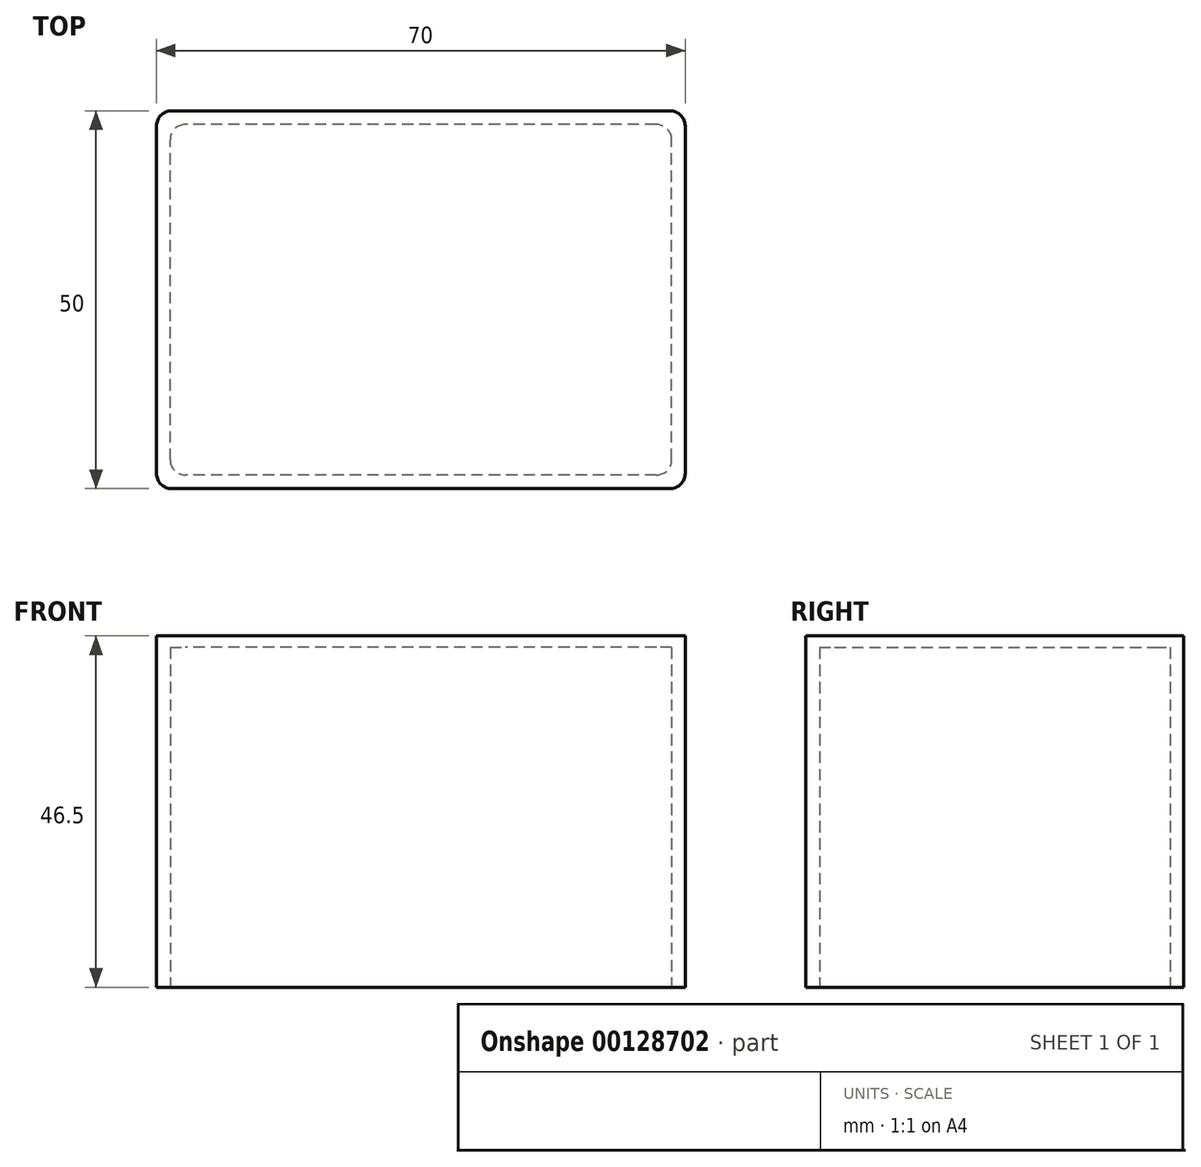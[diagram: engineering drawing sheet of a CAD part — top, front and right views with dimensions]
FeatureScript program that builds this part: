
annotation { "Feature Type Name" : "Feature", "Feature Type Description" : "" }
export const myFeature = defineFeature(function(context is Context, id is Id, definition is map)
    precondition{}
    {
        {
            var Q0;
            Q0=qCreatedBy(makeId("Top.planeOp"),FACE);
            var sketch = newSketch(context, id + "F0", { "sketchPlane" : qUnion([Q0])});
            skLineSegment(sketch, "E0.bottom", {"start": v(33, -25) * mm, "end": v(-33, -25) * mm});
            skLineSegment(sketch, "E0.top", {"start": v(33, 25) * mm, "end": v(-33, 25) * mm});
            skLineSegment(sketch, "E0.left", {"start": v(35, -23) * mm, "end": v(35, 23) * mm});
            skLineSegment(sketch, "E0.right", {"start": v(-35, -23) * mm, "end": v(-35, 23) * mm});
            skPoint(sketch, "E0.middle", {"position": v(0, 0) * mm});
            skLineSegment(sketch, "E1.0", {"start": v(31.2, 23.2) * mm, "end": v(-31.2, 23.2) * mm});
            skLineSegment(sketch, "E1.1", {"start": v(33.2, -21.2) * mm, "end": v(33.2, 21.2) * mm});
            skLineSegment(sketch, "E1.2", {"start": v(31.2, -23.2) * mm, "end": v(-31.2, -23.2) * mm});
            skLineSegment(sketch, "E1.3", {"start": v(-33.2, -21.2) * mm, "end": v(-33.2, 21.2) * mm});
            skPoint(sketch, "E2.visualSharp", {"position": v(-33.2, 23.2) * mm});
            skArc(sketch, "E2.filletArc", {"start": v(-31.2, 23.2) * mm, "mid": v(-32.61, 22.61) * mm, "end": v(-33.2, 21.2) * mm});
            skPoint(sketch, "E3.visualSharp", {"position": v(-35, 25) * mm});
            skArc(sketch, "E3.filletArc", {"start": v(-33, 25) * mm, "mid": v(-34.41, 24.41) * mm, "end": v(-35, 23) * mm});
            skPoint(sketch, "E4.visualSharp", {"position": v(33.2, 23.2) * mm});
            skArc(sketch, "E4.filletArc", {"start": v(33.2, 21.2) * mm, "mid": v(32.61, 22.61) * mm, "end": v(31.2, 23.2) * mm});
            skPoint(sketch, "E5.visualSharp", {"position": v(35, 25) * mm});
            skArc(sketch, "E5.filletArc", {"start": v(35, 23) * mm, "mid": v(34.41, 24.41) * mm, "end": v(33, 25) * mm});
            skPoint(sketch, "E6.visualSharp", {"position": v(33.2, -23.2) * mm});
            skArc(sketch, "E6.filletArc", {"start": v(31.2, -23.2) * mm, "mid": v(32.61, -22.61) * mm, "end": v(33.2, -21.2) * mm});
            skPoint(sketch, "E7.visualSharp", {"position": v(35, -25) * mm});
            skArc(sketch, "E7.filletArc", {"start": v(33, -25) * mm, "mid": v(34.41, -24.41) * mm, "end": v(35, -23) * mm});
            skPoint(sketch, "E8.visualSharp", {"position": v(-33.2, -23.2) * mm});
            skArc(sketch, "E8.filletArc", {"start": v(-33.2, -21.2) * mm, "mid": v(-32.61, -22.61) * mm, "end": v(-31.2, -23.2) * mm});
            skPoint(sketch, "E9.visualSharp", {"position": v(-35, -25) * mm});
            skArc(sketch, "E9.filletArc", {"start": v(-35, -23) * mm, "mid": v(-34.41, -24.41) * mm, "end": v(-33, -25) * mm});
            skSolve(sketch);
        }
        {
            var Q0;
            Q0=makeQuery(id+"F0.imprint","IMPRINT",FACE,{"disambiguationData":[TD([[makeQuery(id+"F0.imprint","IMPRINT",EDGE,{"derivedFrom":sQuery(id+"F0.wireOp",EDGE,"E0.bottom")}),-1.0]])]});
            extrude(context, id + "F1", {"entities" : qUnion([Q0]), "depth" : 45 * mm});
        }
        {
            var Q0;
            Q0=makeQuery(id+"F1.opExtrude","CAP_FACE",FACE,{"disambiguationData":[OSD([sQuery(id+"F0.wireOp",EDGE,"E0.bottom"),sQuery(id+"F0.wireOp",EDGE,"E0.top"),sQuery(id+"F0.wireOp",EDGE,"E0.left"),sQuery(id+"F0.wireOp",EDGE,"E0.right"),sQuery(id+"F0.wireOp",EDGE,"E1.0"),sQuery(id+"F0.wireOp",EDGE,"E1.1"),sQuery(id+"F0.wireOp",EDGE,"E1.2"),sQuery(id+"F0.wireOp",EDGE,"E1.3"),sQuery(id+"F0.wireOp",EDGE,"E2.filletArc"),sQuery(id+"F0.wireOp",EDGE,"E3.filletArc"),sQuery(id+"F0.wireOp",EDGE,"E4.filletArc"),sQuery(id+"F0.wireOp",EDGE,"E5.filletArc"),sQuery(id+"F0.wireOp",EDGE,"E6.filletArc"),sQuery(id+"F0.wireOp",EDGE,"E7.filletArc"),sQuery(id+"F0.wireOp",EDGE,"E8.filletArc"),sQuery(id+"F0.wireOp",EDGE,"E9.filletArc")])],"isStart":false});
            var sketch = newSketch(context, id + "F2", { "sketchPlane" : qUnion([Q0])});
            skLineSegment(sketch, "E10.0", {"start": v(33, 25) * mm, "end": v(-33, 25) * mm});
            skArc(sketch, "E10.1", {"start": v(-33, 25) * mm, "mid": v(-34.41, 24.41) * mm, "end": v(-35, 23) * mm});
            skLineSegment(sketch, "E10.2", {"start": v(-35, -23) * mm, "end": v(-35, 23) * mm});
            skArc(sketch, "E10.3", {"start": v(-35, -23) * mm, "mid": v(-34.41, -24.41) * mm, "end": v(-33, -25) * mm});
            skLineSegment(sketch, "E10.4", {"start": v(33, -25) * mm, "end": v(-33, -25) * mm});
            skArc(sketch, "E10.5", {"start": v(33, -25) * mm, "mid": v(34.41, -24.41) * mm, "end": v(35, -23) * mm});
            skLineSegment(sketch, "E10.6", {"start": v(35, -23) * mm, "end": v(35, 23) * mm});
            skArc(sketch, "E10.7", {"start": v(35, 23) * mm, "mid": v(34.41, 24.41) * mm, "end": v(33, 25) * mm});
            skSolve(sketch);
        }
        {
            var Q0;
            Q0 = qSketchRegion(id + "F2", true);
            extrude(context, id + "F3", {"entities" : qUnion([Q0]), "operationType" : NewBodyOperationType.ADD, "depth" : 1.5 * mm});
        }
    });
